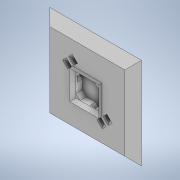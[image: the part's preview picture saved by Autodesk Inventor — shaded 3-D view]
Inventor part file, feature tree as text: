
AUTODESK INVENTOR PART (.ipt)
format: ipt  version: 2021 (Build 250183000, 183)  size: 206,848 bytes
history: native  units: in
note: dims shown in document units (in); Inventor stores cm internally (conversion verified against a paired STEP export)
features: sketch x5, extrude x3, plane x3, chamfer x2, projected_geometry x2, sweep x1, mirror x1
ambient origin geometry x8: Origin, YZ Plane, XZ Plane, XY Plane, X Axis, Y Axis, Z Axis, Center Point
bodies: Solid1 (feature_tree)
feature tree (17):
  extrude  "Extrusion1"  Depth=0.1575in
  chamfer  "Chamfer1"  Distance=0.1575in
  extrude  "Extrusion2"  Depth=0.1181in TaperAngle=0.0deg
  plane  "Work Plane3"
  plane  "Work Plane4"
  plane  "Work Plane5"
  sweep  "Sweep3"
  mirror  "Mirror2"
  extrude  "Extrusion7"  Depth=0.0984in
  chamfer  "Chamfer6"  Distance=0.0492in
  sketch  "Sketch1"  dims[d0=1.7323in d1=1.7323in d2=0.1575in d3=0.0in]
  sketch  "Sketch2"  dims[d4=0.1575in d5=0.0787in d6=45.0deg d8=0.1181in d9=0.0in]
  projected_geometry  "Projected Loop1"
  sketch  "Sketch13"  dims[d86=0.0787in d87=0.0787in]
  sketch  "Sketch14"  dims[d88=0.0492in d89=0.0984in]
  sketch  "Sketch15"  dims[d90=0.0984in d91=0.0492in d92=0.3937in d93=45.0deg d94=0.3937in d95=0.0in d96=0.0in d97=0.0591in d98=0.0591in d99=0.0in d100=0.0591in d101=0.0787in d102=45.0deg]
  projected_geometry  "Projected Loop6"
